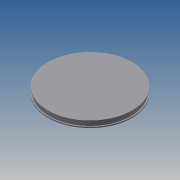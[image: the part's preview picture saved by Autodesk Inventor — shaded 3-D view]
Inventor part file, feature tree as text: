
AUTODESK INVENTOR PART (.ipt)
format: ipt  version: 2013 (Build 170138000, 138)  size: 99,328 bytes
history: native  units: mm
features: extrude x4, sketch x4
ambient origin geometry x8: Origin, YZ Plane, XZ Plane, XY Plane, X Axis, Y Axis, Z Axis, Center Point
bodies: Solid1 (feature_tree)
feature tree (8):
  extrude  "Extrusion1"  Depth=2.0mm TaperAngle=0.0deg
  extrude  "Extrusion2"  Depth=8.0mm TaperAngle=0.0deg
  extrude  "Extrusion3"  Depth=12.5mm
  extrude  "Extrusion4"  [1 undecoded]
  sketch  "Sketch1"  dims[d0=154.0mm d2=2.0mm d3=0.0mm]
  sketch  "Sketch2"  dims[d4=150.0mm d6=8.0mm d7=0.0mm]
  sketch  "Sketch3"  dims[d8=2.0mm d9=0.0mm d10=12.5mm]
  sketch  "Sketch4"  dims[d12=2.0mm d13=0.0mm]
note: 1 required parameter value undecoded (feature->parameter linkage not recoverable at this tier; creation-order binding heuristic only, values carry confidence <= 0.55)
